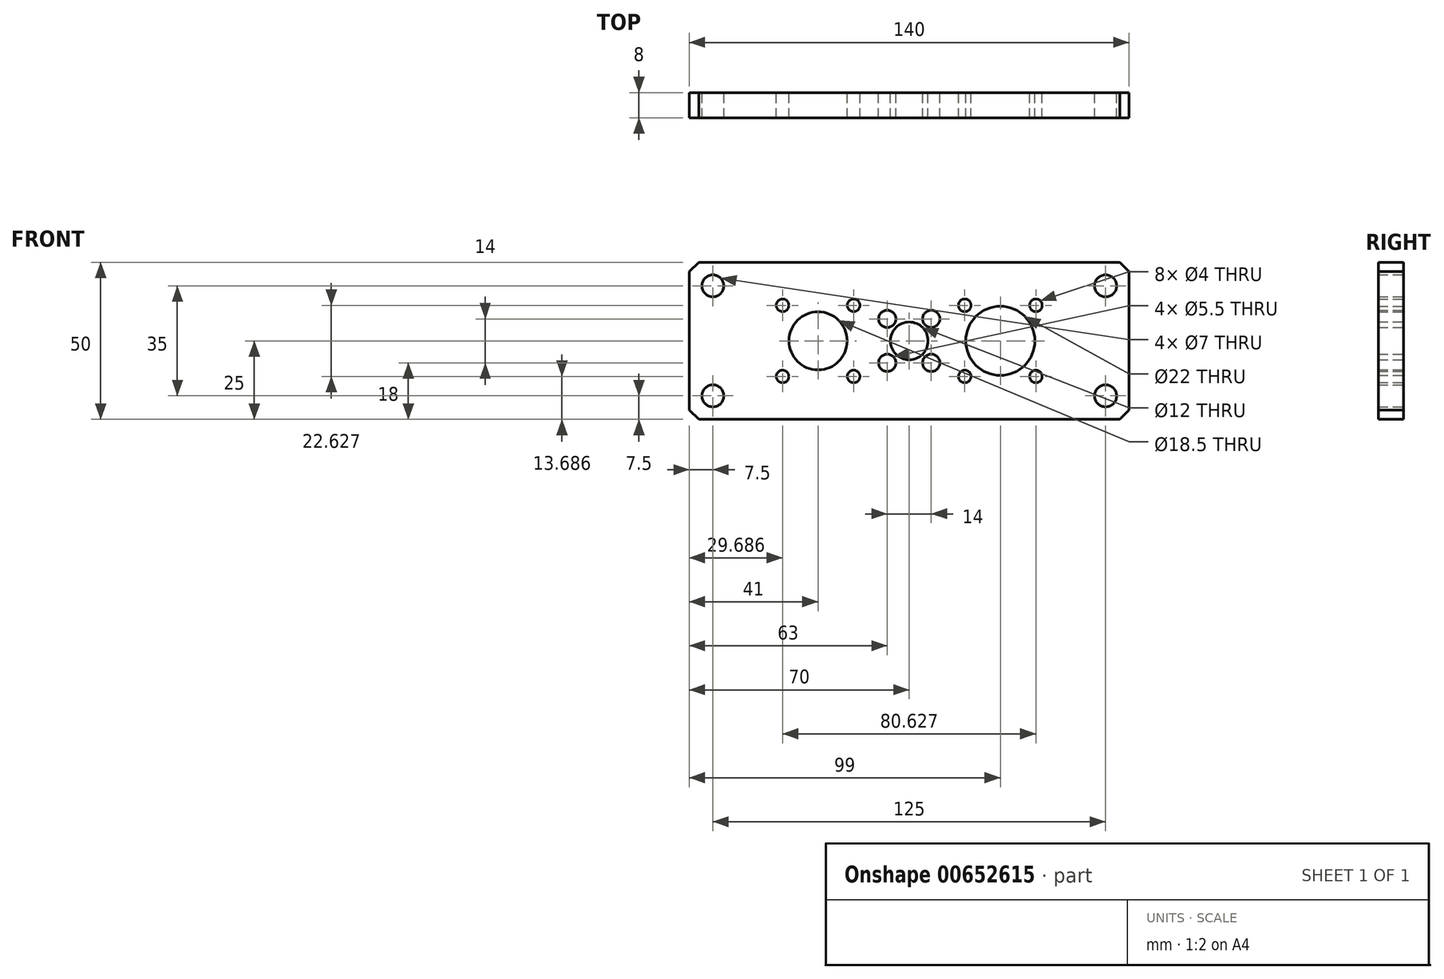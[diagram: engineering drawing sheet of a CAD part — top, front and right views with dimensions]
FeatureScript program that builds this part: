
annotation { "Feature Type Name" : "Feature", "Feature Type Description" : "" }
export const myFeature = defineFeature(function(context is Context, id is Id, definition is map)
    precondition{}
    {
        {
            var Q0;
            Q0=qCreatedBy(makeId("Front.planeOp"),FACE);
            var sketch = newSketch(context, id + "F0", { "sketchPlane" : qUnion([Q0])});
            skLineSegment(sketch, "E0.bottom", {"start": v(0, 0) * mm, "end": v(140, 0) * mm});
            skLineSegment(sketch, "E0.top", {"start": v(0, 50) * mm, "end": v(140, 50) * mm});
            skLineSegment(sketch, "E0.left", {"start": v(0, 0) * mm, "end": v(0, 50) * mm});
            skLineSegment(sketch, "E0.right", {"start": v(140, 0) * mm, "end": v(140, 50) * mm});
            skCircle(sketch, "E1", {"center": v(7.5, 42.5) * mm, "radius": 3.5 * mm});
            skCircle(sketch, "E2", {"center": v(7.5, 7.5) * mm, "radius": 3.5 * mm});
            skCircle(sketch, "E3", {"center": v(132.5, 7.5) * mm, "radius": 3.5 * mm});
            skCircle(sketch, "E4", {"center": v(132.5, 42.5) * mm, "radius": 3.5 * mm});
            skCircle(sketch, "E5", {"center": v(41, 25) * mm, "radius": 9.25 * mm});
            skCircle(sketch, "E6", {"center": v(70, 25) * mm, "radius": 6 * mm});
            skCircle(sketch, "E7", {"center": v(63, 18) * mm, "radius": 2.75 * mm});
            skCircle(sketch, "E8", {"center": v(63, 32) * mm, "radius": 2.75 * mm});
            skCircle(sketch, "E9", {"center": v(77, 32) * mm, "radius": 2.75 * mm});
            skCircle(sketch, "E10", {"center": v(77, 18) * mm, "radius": 2.75 * mm});
            skCircle(sketch, "E11", {"center": v(29.69, 36.31) * mm, "radius": 2 * mm});
            skCircle(sketch, "E12", {"center": v(99, 25) * mm, "radius": 11 * mm});
            skCircle(sketch, "E13.1.0", {"center": v(29.69, 13.69) * mm, "radius": 2 * mm});
            skCircle(sketch, "E13.2.0", {"center": v(52.31, 13.69) * mm, "radius": 2 * mm});
            skCircle(sketch, "E13.3.0", {"center": v(52.31, 36.31) * mm, "radius": 2 * mm});
            skCircle(sketch, "E14.MirrorC", {"center": v(87.69, 36.31) * mm, "radius": 2 * mm});
            skCircle(sketch, "E15.MirrorC", {"center": v(110.31, 36.31) * mm, "radius": 2 * mm});
            skCircle(sketch, "E16.MirrorC", {"center": v(110.31, 13.69) * mm, "radius": 2 * mm});
            skCircle(sketch, "E17.MirrorC", {"center": v(87.69, 13.69) * mm, "radius": 2 * mm});
            skSolve(sketch);
        }
        {
            var Q0;
            Q0=makeQuery(id+"F0.imprint","IMPRINT",FACE,{"disambiguationData":[TD([[makeQuery(id+"F0.imprint","IMPRINT",EDGE,{"derivedFrom":sQuery(id+"F0.wireOp",EDGE,"E0.bottom")}),1.0]])]});
            var Q1;
            Q1=makeQuery(id+"F0.imprint","IMPRINT",FACE,{"disambiguationData":[TD([[makeQuery(id+"F0.imprint","IMPRINT",EDGE,{"derivedFrom":sQuery(id+"F0.wireOp",EDGE,"E13.3.0")}),1.0]])]});
            var Q2;
            Q2=makeQuery(id+"F0.imprint","IMPRINT",FACE,{"disambiguationData":[TD([[makeQuery(id+"F0.imprint","IMPRINT",EDGE,{"derivedFrom":sQuery(id+"F0.wireOp",EDGE,"E11")}),1.0]])]});
            var Q3;
            Q3=makeQuery(id+"F0.imprint","IMPRINT",FACE,{"disambiguationData":[TD([[makeQuery(id+"F0.imprint","IMPRINT",EDGE,{"derivedFrom":sQuery(id+"F0.wireOp",EDGE,"E13.1.0")}),1.0]])]});
            var Q4;
            Q4=makeQuery(id+"F0.imprint","IMPRINT",FACE,{"disambiguationData":[TD([[makeQuery(id+"F0.imprint","IMPRINT",EDGE,{"derivedFrom":sQuery(id+"F0.wireOp",EDGE,"E13.2.0")}),1.0]])]});
            var Q5;
            Q5=makeQuery(id+"F0.imprint","IMPRINT",FACE,{"disambiguationData":[TD([[makeQuery(id+"F0.imprint","IMPRINT",EDGE,{"derivedFrom":sQuery(id+"F0.wireOp",EDGE,"E17.MirrorC")}),-1.0]])]});
            var Q6;
            Q6=makeQuery(id+"F0.imprint","IMPRINT",FACE,{"disambiguationData":[TD([[makeQuery(id+"F0.imprint","IMPRINT",EDGE,{"derivedFrom":sQuery(id+"F0.wireOp",EDGE,"E16.MirrorC")}),-1.0]])]});
            var Q7;
            Q7=makeQuery(id+"F0.imprint","IMPRINT",FACE,{"disambiguationData":[TD([[makeQuery(id+"F0.imprint","IMPRINT",EDGE,{"derivedFrom":sQuery(id+"F0.wireOp",EDGE,"E15.MirrorC")}),-1.0]])]});
            var Q8;
            Q8=makeQuery(id+"F0.imprint","IMPRINT",FACE,{"disambiguationData":[TD([[makeQuery(id+"F0.imprint","IMPRINT",EDGE,{"derivedFrom":sQuery(id+"F0.wireOp",EDGE,"E14.MirrorC")}),-1.0]])]});
            extrude(context, id + "F1", {"entities" : qUnion([Q0, Q1, Q2, Q3, Q4, Q5, Q6, Q7, Q8]), "depth" : 8 * mm, "offsetDistance" : 25 * mm});
        }
        {
            var Q0;
            Q0=sQuery(id+"F0.wireOp",VERTEX,"E11.center");
            var Q1;
            Q1=sQuery(id+"F0.wireOp",VERTEX,"E13.1.0.center");
            var Q2;
            Q2=sQuery(id+"F0.wireOp",VERTEX,"E13.2.0.center");
            var Q3;
            Q3=sQuery(id+"F0.wireOp",VERTEX,"E13.3.0.center");
            var Q4;
            Q4=sQuery(id+"F0.wireOp",VERTEX,"E14.MirrorC.center");
            var Q5;
            Q5=sQuery(id+"F0.wireOp",VERTEX,"E17.MirrorC.center");
            var Q6;
            Q6=sQuery(id+"F0.wireOp",VERTEX,"E16.MirrorC.center");
            var Q7;
            Q7=sQuery(id+"F0.wireOp",VERTEX,"E15.MirrorC.center");
            var Q8;
            Q8=makeQuery(id+"F1.opExtrude","SWEPT_BODY",BODY,{"disambiguationData":[OSD([sQuery(id+"F0.wireOp",EDGE,"E0.bottom"),sQuery(id+"F0.wireOp",EDGE,"E0.top"),sQuery(id+"F0.wireOp",EDGE,"E0.left"),sQuery(id+"F0.wireOp",EDGE,"E0.right"),sQuery(id+"F0.wireOp",EDGE,"E1"),sQuery(id+"F0.wireOp",EDGE,"E2"),sQuery(id+"F0.wireOp",EDGE,"E3"),sQuery(id+"F0.wireOp",EDGE,"E4"),sQuery(id+"F0.wireOp",EDGE,"E5"),sQuery(id+"F0.wireOp",EDGE,"E6"),sQuery(id+"F0.wireOp",EDGE,"E7"),sQuery(id+"F0.wireOp",EDGE,"E8"),sQuery(id+"F0.wireOp",EDGE,"E9"),sQuery(id+"F0.wireOp",EDGE,"E10"),sQuery(id+"F0.wireOp",EDGE,"E12")])]});
            hole(context, id + "F2", {"style" : HoleStyle.SIMPLE, "endStyle" : HoleEndStyle.THROUGH, "oppositeDirection" : true, "holeDiameter" : 4 * mm, "majorDiameter" : 5 * mm, "isTappedThrough" : true, "tappedDepth" : 12 * mm, "tapClearance" : 3, "locations" : qUnion([Q0, Q1, Q2, Q3, Q4, Q5, Q6, Q7]), "scope" : qUnion([Q8])});
        }
        {
            var Q0;
            Q0=makeQuery(id+"F1.opExtrude","SWEPT_EDGE",EDGE,{"disambiguationData":[OSD([sQuery(id+"F0.wireOp",EDGE,"E0.top"),sQuery(id+"F0.wireOp",EDGE,"E0.right")])]});
            var Q1;
            Q1=makeQuery(id+"F1.opExtrude","SWEPT_EDGE",EDGE,{"disambiguationData":[OSD([sQuery(id+"F0.wireOp",EDGE,"E0.bottom"),sQuery(id+"F0.wireOp",EDGE,"E0.right")])]});
            var Q2;
            Q2=makeQuery(id+"F1.opExtrude","SWEPT_EDGE",EDGE,{"disambiguationData":[OSD([sQuery(id+"F0.wireOp",EDGE,"E0.bottom"),sQuery(id+"F0.wireOp",EDGE,"E0.left")])]});
            var Q3;
            Q3=makeQuery(id+"F1.opExtrude","SWEPT_EDGE",EDGE,{"disambiguationData":[OSD([sQuery(id+"F0.wireOp",EDGE,"E0.top"),sQuery(id+"F0.wireOp",EDGE,"E0.left")])]});
            chamfer(context, id + "F3", {"entities" : qUnion([Q0, Q1, Q2, Q3]), "width" : 3 * mm, "tangentPropagation" : true});
        }
    });
